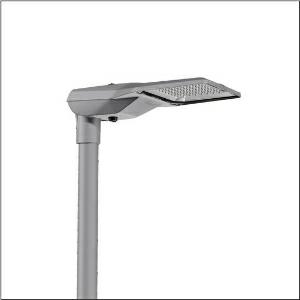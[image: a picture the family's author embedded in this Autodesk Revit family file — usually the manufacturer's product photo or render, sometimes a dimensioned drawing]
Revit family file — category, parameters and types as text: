
# Revit family: streetlight_sl_21_midi___st1_5a_5xe3p43t08mb_72ce
name_source: partatom
category: Lighting Fixtures
units: mm (PartAtom-declared; Revit-internal decimal feet)

## family parameters
Cut with Voids When Loaded = No
Host = Face
Light Source = No
Part Type = Normal
Room Calculation Point = No
Round Connector Dimension = Use Diameter
Shared = No

## types (1)
- --- (1 x LED, 19830 lm, 147 W, 4000K)
    Apparent Load = 147 VA
    CIE Flux Codes = 22 53 95 100 100
    Color Rendering = 70
    Color Temperature = 4000K
    Default Elevation = 1800 mm
    Description = Streetlight SL 21 midi, mast luminaire, primary light control with lens, of PMMA, primary optical cover: cover, of toughened safety glass, transparent, light distribution: ST1.5a, light emission: direct distribution, primary light characteristic: asymmetric, installation type: side-entry, post-top, LED, High Power LED, rated luminous flux: 19.830lm, luminous efficacy: 135lm/W, light colour: 740, colour temperature: 4000K, control gear: D4i, control: overheat protection, constant luminous flux control, time-dependent luminous flux control, flexible luminous flux parameterisation, pre-setting: logarithmic dimming characteristic, mains connection: 230..240V, AC, 50/60Hz, start of lifetime: 147W, end of service life: 155W, reduction: 65W, luminaire housing, of diecast aluminium, powder-coated, Siteco® metallic grey (DB 702S), corrosivity category C5 mid according to DIN EN ISO 12944, please order mast flange separately, inclination adjustable: 0°, 5°, 10°, 15°, sealing non-destructively replaceable, multi-level sealing system, length: 644mm, width: 335mm, height: 110mm, mast flange for spigot size: 42mm (side-entry): 5XC10008XM4, 60/48mm (side-entry/post-top): 5XC10108XM2, 76/60mm (side-entry/post-top): 5XC10108XM1, mounting height: 4..8m, Smart Interface below and above, protection rating (complete): IP66, insulation class (complete): insulation class II (safety insulation), certification: CE, ENEC, ENEC+, VDE, impact resistance: IK10, permissible operating ambient temperature for outdoor applications: -40..+50°C, standard-compliant lighting for roads and squares, packaging unit: 1 piece

Light Distribution: ST1.5a
    Height = 111 mm
    Lamp = 1 x LED
    Lamp Light Flux = 19830 lm
    Lamp Power = 147 W
    Lamp count = 1
    Length = 644 mm
    Luminous efficacy = 135 lm/W
    Manufacturer = Siteco
    ModVariant = No
    Model = 5XE3P43T08MB
    Number of Poles = 1
    OnlyDefault = Yes
    Power Factor = 1
    Product Name = Streetlight SL 21 midi | ST1.5a
    Product group = mast luminaire | pylon top
    ProductGroupID = 6100
    Protection Class = Protection class II
    Protection Degree = IP 66
    RLX_Detail_Level = 1
    RLX_Emergency_Light_Flux = 0 lm
    RLX_Emergency_Type = 0
    RLX_Emergency_Type_DB = No
    RlxData = <blob elided: 30513 chars, md5=6ac6bb14>
    Socket = socket
    Standby Power = 0 W
    System Light Flux = 19830 lm
    System Power = 147 W
    Type Comments = factory setting: luminous flux: 100 % | dim-lin: 254 | 750 mA
    Type Image = l_1004304.jpg
    URL = http://relux.com
    VarID = @adj_197533
    Voltage = 0 V
    Weight = 0.00 kg
    Width = 336 mm

## geometry (parser evidence)
native form markers: Blend x4, Sweep x9
no freeform markers — native parametric forms only
